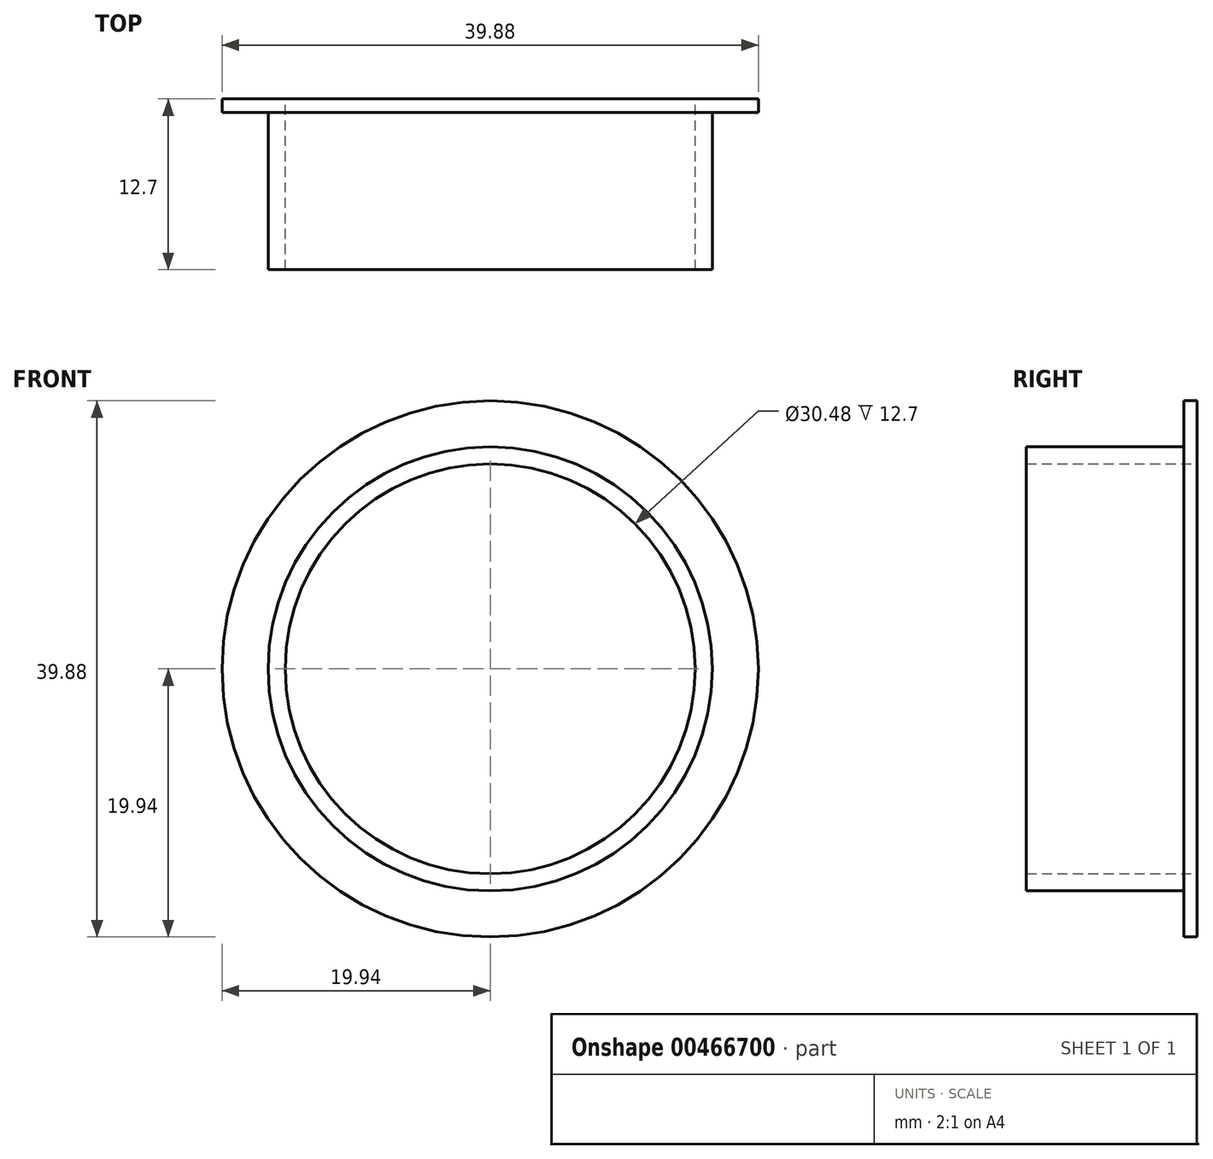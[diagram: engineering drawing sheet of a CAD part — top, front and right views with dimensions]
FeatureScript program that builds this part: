
annotation { "Feature Type Name" : "Feature", "Feature Type Description" : "" }
export const myFeature = defineFeature(function(context is Context, id is Id, definition is map)
    precondition{}
    {
        {
            var Q0;
            Q0=qCreatedBy(makeId("Front.planeOp"),FACE);
            var sketch = newSketch(context, id + "F0", { "sketchPlane" : qUnion([Q0])});
            skCircle(sketch, "E0", {"center": v(0, 0) * mm, "radius": 19.94 * mm});
            skCircle(sketch, "E1", {"center": v(0, 0) * mm, "radius": 16.51 * mm});
            skCircle(sketch, "E2", {"center": v(0, 0) * mm, "radius": 15.24 * mm});
            skSolve(sketch);
        }
        {
            var Q0;
            Q0 = qSketchRegion(id + "F0", true);
            extrude(context, id + "F1", {"entities" : qUnion([Q0]), "depth" : 1 * mm});
        }
        {
            var Q0;
            Q0=qCreatedBy(makeId("Front.planeOp"),FACE);
            var sketch = newSketch(context, id + "F2", { "sketchPlane" : qUnion([Q0])});
            skCircle(sketch, "E3", {"center": v(0, 0) * mm, "radius": 15.24 * mm});
            skCircle(sketch, "E4", {"center": v(0, 0) * mm, "radius": 16.51 * mm});
            skSolve(sketch);
        }
        {
            var Q0;
            Q0 = qSketchRegion(id + "F2", true);
            extrude(context, id + "F3", {"entities" : qUnion([Q0]), "operationType" : NewBodyOperationType.ADD, "depth" : 12.7 * mm});
        }
    });
